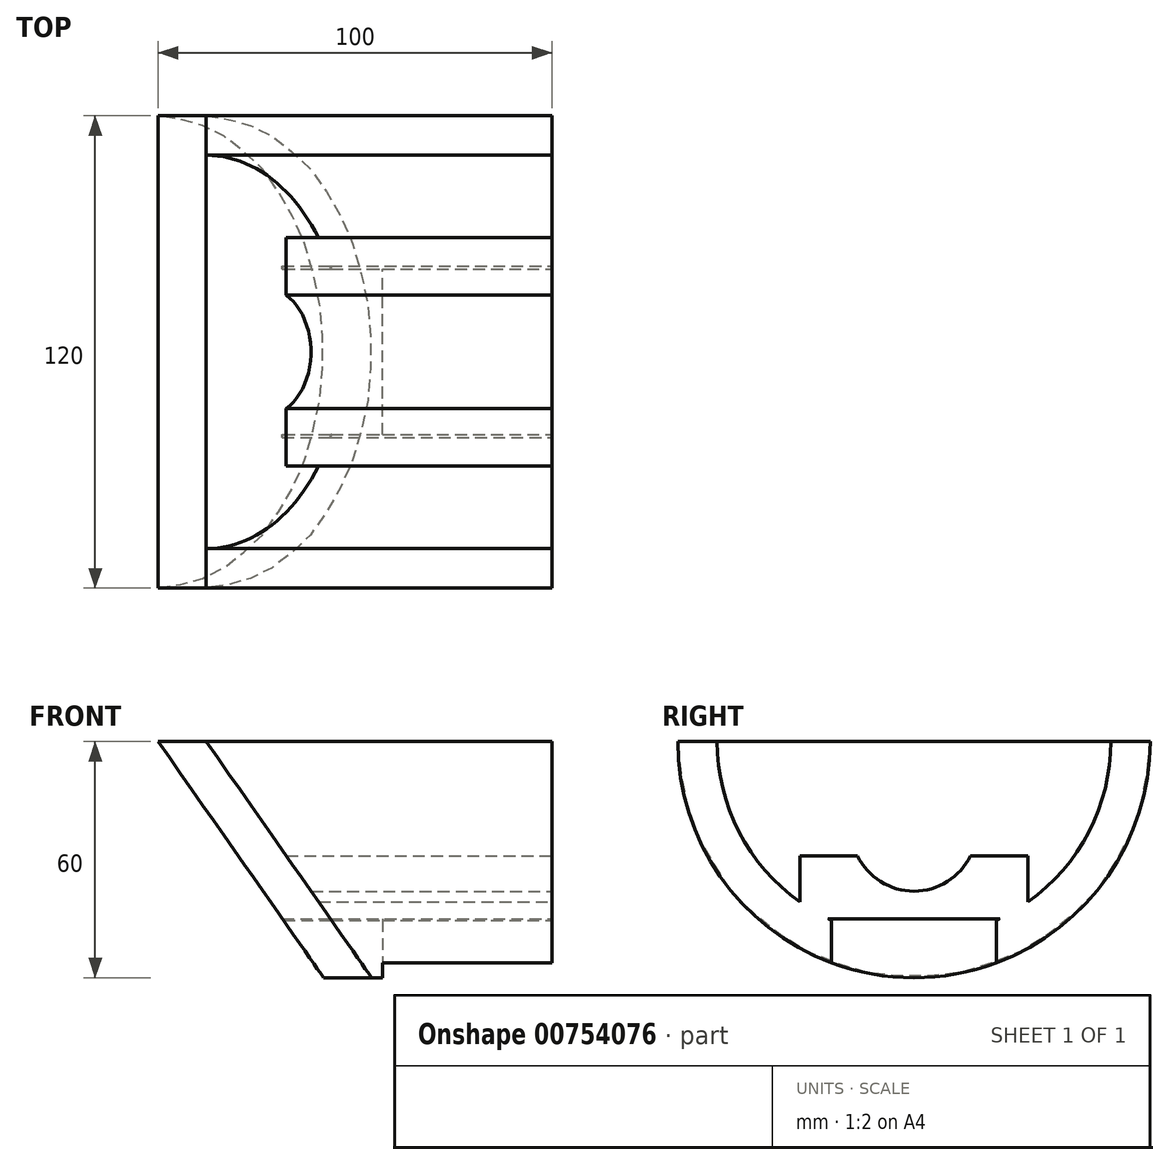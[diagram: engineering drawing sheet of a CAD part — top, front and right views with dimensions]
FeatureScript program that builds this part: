
annotation { "Feature Type Name" : "Feature", "Feature Type Description" : "" }
export const myFeature = defineFeature(function(context is Context, id is Id, definition is map)
    precondition{}
    {
        {
            var Q0;
            Q0=qCreatedBy(makeId("Right.planeOp"),FACE);
            var sketch = newSketch(context, id + "F0", { "sketchPlane" : qUnion([Q0])});
            skArc(sketch, "E0", {"start": v(-60, 0) * mm, "mid": v(0, -60) * mm, "end": v(60, 0) * mm});
            skArc(sketch, "E1", {"start": v(-50, 0) * mm, "mid": v(0, -50) * mm, "end": v(50, 0) * mm});
            skCircle(sketch, "E2", {"center": v(0, -22) * mm, "radius": 16 * mm});
            skLineSegment(sketch, "E3", {"start": v(-68.18, 0) * mm, "end": v(68.4, 0) * mm});
            skLineSegment(sketch, "E4", {"start": v(-38.6, -29) * mm, "end": v(41.93, -29) * mm});
            skLineSegment(sketch, "E5", {"start": v(-26.14, -45) * mm, "end": v(26.36, -45) * mm});
            skLineSegment(sketch, "E6", {"start": v(21, -45) * mm, "end": v(21, -63.96) * mm});
            skLineSegment(sketch, "E7", {"start": v(-21, -45) * mm, "end": v(-21, -64.85) * mm});
            skLineSegment(sketch, "E8", {"start": v(29, -29) * mm, "end": v(29, -49.1) * mm});
            skLineSegment(sketch, "E9", {"start": v(-29, -29) * mm, "end": v(-29, -49.67) * mm});
            skSolve(sketch);
        }
        {
            var Q0;
            {var subQ4=sQuery(id+"F0.wireOp",EDGE,"E0");var subQ7=sQuery(id+"F0.wireOp",EDGE,"E3");var subQ9=makeQuery(id+"F0.imprint","INTERSECT",VERTEX,{"disambiguationData":[OD(0.0)],"derivedFrom":[subQ4,subQ7]});Q0=makeQuery(id+"F0.imprint","IMPRINT",FACE,{"disambiguationData":[TD([[makeQuery(id+"F0.imprint","IMPRINT",EDGE,{"disambiguationData":[TD([[subQ9,-1.0]])],"derivedFrom":subQ4}),1.0]])]});}
            var Q1;
            {var subQ0=sQuery(id+"F0.wireOp",EDGE,"E9");var subQ7=sQuery(id+"F0.wireOp",EDGE,"E1");var subQ13=makeQuery(id+"F0.imprint","INTERSECT",VERTEX,{"derivedFrom":[subQ7,subQ0]});Q1=makeQuery(id+"F0.imprint","IMPRINT",FACE,{"disambiguationData":[TD([[makeQuery(id+"F0.imprint","IMPRINT",EDGE,{"disambiguationData":[TD([[subQ13,-1.0]])],"derivedFrom":subQ7}),1.0]])]});}
            var Q2;
            {var subQ6=sQuery(id+"F0.wireOp",EDGE,"E3");var subQ7=sQuery(id+"F0.wireOp",EDGE,"E0");var subQ8=makeQuery(id+"F0.imprint","INTERSECT",VERTEX,{"disambiguationData":[OD(1.0)],"derivedFrom":[subQ7,subQ6]});Q2=makeQuery(id+"F0.imprint","IMPRINT",FACE,{"disambiguationData":[TD([[makeQuery(id+"F0.imprint","IMPRINT",EDGE,{"disambiguationData":[TD([[subQ8,1.0]])],"derivedFrom":subQ7}),1.0]])]});}
            var Q3;
            {var subQ0=sQuery(id+"F0.wireOp",EDGE,"E5");var subQ1=sQuery(id+"F0.wireOp",EDGE,"E1");var subQ2=makeQuery(id+"F0.imprint","INTERSECT",VERTEX,{"disambiguationData":[OD(1.0)],"derivedFrom":[subQ1,subQ0]});Q3=makeQuery(id+"F0.imprint","IMPRINT",FACE,{"disambiguationData":[TD([[makeQuery(id+"F0.imprint","IMPRINT",EDGE,{"disambiguationData":[TD([[subQ2,1.0]])],"derivedFrom":subQ1}),1.0]])]});}
            var Q4;
            {var subQ0=sQuery(id+"F0.wireOp",EDGE,"E5");var subQ1=sQuery(id+"F0.wireOp",EDGE,"E1");var subQ2=makeQuery(id+"F0.imprint","INTERSECT",VERTEX,{"disambiguationData":[OD(0.0)],"derivedFrom":[subQ1,subQ0]});Q4=makeQuery(id+"F0.imprint","IMPRINT",FACE,{"disambiguationData":[TD([[makeQuery(id+"F0.imprint","IMPRINT",EDGE,{"disambiguationData":[TD([[subQ2,-1.0]])],"derivedFrom":subQ1}),1.0]])]});}
            var Q5;
            {var subQ0=sQuery(id+"F0.wireOp",EDGE,"E7");var subQ1=sQuery(id+"F0.wireOp",EDGE,"E1");var subQ2=makeQuery(id+"F0.imprint","INTERSECT",VERTEX,{"derivedFrom":[subQ1,subQ0]});Q5=makeQuery(id+"F0.imprint","IMPRINT",FACE,{"disambiguationData":[TD([[makeQuery(id+"F0.imprint","IMPRINT",EDGE,{"disambiguationData":[TD([[subQ2,-1.0]])],"derivedFrom":subQ1}),1.0]])]});}
            var Q6;
            {var subQ0=sQuery(id+"F0.wireOp",EDGE,"E7");var subQ1=sQuery(id+"F0.wireOp",EDGE,"E0");var subQ2=makeQuery(id+"F0.imprint","INTERSECT",VERTEX,{"derivedFrom":[subQ1,subQ0]});Q6=makeQuery(id+"F0.imprint","IMPRINT",FACE,{"disambiguationData":[TD([[makeQuery(id+"F0.imprint","IMPRINT",EDGE,{"disambiguationData":[TD([[subQ2,-1.0]])],"derivedFrom":subQ1}),1.0]])]});}
            extrude(context, id + "F1", {"entities" : qUnion([Q0, Q1, Q2, Q3, Q4, Q5, Q6]), "depth" : -100 * mm, "offsetDistance" : 25 * mm});
        }
        {
            var Q0;
            Q0=qCreatedBy(makeId("Front.planeOp"),FACE);
            var sketch = newSketch(context, id + "F2", { "sketchPlane" : qUnion([Q0])});
            skLineSegment(sketch, "E10.0", {"start": v(-100, 0) * mm, "end": v(0, 0) * mm});
            skLineSegment(sketch, "E11", {"start": v(-100, 0) * mm, "end": v(-56.9, -61.57) * mm});
            skLineSegment(sketch, "E12", {"start": v(0, -60) * mm, "end": v(-100, -60) * mm});
            skLineSegment(sketch, "E13.0", {"start": v(-91.8, 5.74) * mm, "end": v(-41.52, -66.08) * mm});
            skLineSegment(sketch, "E14", {"start": v(-41.52, -66.08) * mm, "end": v(-123.05, -66.08) * mm});
            skLineSegment(sketch, "E15", {"start": v(-123.05, -66.08) * mm, "end": v(-123.05, 5.74) * mm});
            skLineSegment(sketch, "E16", {"start": v(-123.05, 5.74) * mm, "end": v(-91.8, 5.74) * mm});
            skSolve(sketch);
        }
        {
            var Q0;
            {var subQ9=sQuery(id+"F2.wireOp",EDGE,"E14");Q0=makeQuery(id+"F2.imprint","IMPRINT",FACE,{"disambiguationData":[TD([[makeQuery(id+"F2.imprint","IMPRINT",EDGE,{"derivedFrom":subQ9}),-1.0]])]});}
            var Q1;
            {var subQ0=sQuery(id+"F2.wireOp",EDGE,"E11");var subQ1=sQuery(id+"F2.wireOp",EDGE,"E10.0");var subQ2=makeQuery(id+"F2.imprint","INTERSECT",VERTEX,{"derivedFrom":[subQ1,subQ0]});Q1=makeQuery(id+"F2.imprint","IMPRINT",FACE,{"disambiguationData":[TD([[makeQuery(id+"F2.imprint","IMPRINT",EDGE,{"disambiguationData":[TD([[subQ2,-1.0]])],"derivedFrom":subQ1}),-1.0]])]});}
            extrude(context, id + "F3", {"entities" : qUnion([Q0, Q1]), "operationType" : NewBodyOperationType.REMOVE, "oppositeDirection" : true, "depth" : 79.9 * mm, "offsetDistance" : 25 * mm, "hasSecondDirection" : true, "secondDirectionOppositeDirection" : false, "secondDirectionDepth" : 98 * mm});
        }
        {
            var Q0;
            {var subQ0=sQuery(id+"F0.wireOp",EDGE,"E3");Q0=makeQuery(id+"F3.boolean.opBoolean","INTERSECT",EDGE,{"derivedFrom":[makeQuery(id+"F1.opExtrude","SWEPT_FACE",FACE,{"disambiguationData":[OSD([subQ0]),TDD([makeQuery(id+"F0.imprint","IMPRINT",EDGE,{"disambiguationData":[TD([[makeQuery(id+"F0.imprint","INTERSECT",VERTEX,{"disambiguationData":[OD(1.0)],"derivedFrom":[sQuery(id+"F0.wireOp",EDGE,"E0"),subQ0]}),1.0]])],"derivedFrom":subQ0})])]}),makeQuery(id+"F3.opExtrude","SWEPT_FACE",FACE,{"disambiguationData":[OSD([sQuery(id+"F2.wireOp",EDGE,"E13.0")])]})]});}
            cPlane(context, id + "F4", {"entities" : qUnion([Q0]), "cplaneType" : CPlaneType.LINE_ANGLE, "offset" : 25 * mm, "angle" : 125 * degree, "oppositeDirection" : true, "width" : 150 * mm, "height" : 150 * mm});
        }
        {
            var Q0;
            Q0=qCreatedBy(makeId("Front.planeOp"),FACE);
            var sketch = newSketch(context, id + "F5", { "sketchPlane" : qUnion([Q0])});
            skLineSegment(sketch, "E17.0", {"start": v(-91.8, 5.74) * mm, "end": v(-41.52, -66.08) * mm});
            skLineSegment(sketch, "E18.0", {"start": v(-100, 0) * mm, "end": v(-56.9, -61.57) * mm});
            skLineSegment(sketch, "E19", {"start": v(-56.9, -61.57) * mm, "end": v(-53.73, -66.08) * mm});
            skLineSegment(sketch, "E20", {"start": v(-53.73, -66.08) * mm, "end": v(-41.52, -66.08) * mm});
            skLineSegment(sketch, "E21", {"start": v(-100, 0) * mm, "end": v(-104.02, 5.74) * mm});
            skLineSegment(sketch, "E22", {"start": v(-104.02, 5.74) * mm, "end": v(-91.8, 5.74) * mm});
            skSolve(sketch);
        }
        {
            var Q0;
            Q0=makeQuery(id+"F5.imprint","IMPRINT",FACE,{"disambiguationData":[TD([[makeQuery(id+"F5.imprint","IMPRINT",EDGE,{"derivedFrom":sQuery(id+"F5.wireOp",EDGE,"E17.0")}),-1.0]])]});
            extrude(context, id + "F6", {"entities" : qUnion([Q0]), "depth" : 74.8 * mm, "offsetDistance" : 25 * mm, "hasSecondDirection" : true, "secondDirectionOppositeDirection" : true, "secondDirectionDepth" : 93.6 * mm});
        }
        {
            var Q0;
            {var subQ4=sQuery(id+"F0.wireOp",EDGE,"E0");var subQ7=sQuery(id+"F0.wireOp",EDGE,"E3");var subQ9=makeQuery(id+"F0.imprint","INTERSECT",VERTEX,{"disambiguationData":[OD(0.0)],"derivedFrom":[subQ4,subQ7]});Q0=makeQuery(id+"F0.imprint","IMPRINT",FACE,{"disambiguationData":[TD([[makeQuery(id+"F0.imprint","IMPRINT",EDGE,{"disambiguationData":[TD([[subQ9,-1.0]])],"derivedFrom":subQ4}),1.0]])]});}
            var Q1;
            {var subQ0=sQuery(id+"F0.wireOp",EDGE,"E3");var subQ1=sQuery(id+"F0.wireOp",EDGE,"E1");var subQ2=makeQuery(id+"F0.imprint","INTERSECT",VERTEX,{"disambiguationData":[OD(0.0)],"derivedFrom":[subQ1,subQ0]});Q1=makeQuery(id+"F0.imprint","IMPRINT",FACE,{"disambiguationData":[TD([[makeQuery(id+"F0.imprint","IMPRINT",EDGE,{"disambiguationData":[TD([[subQ2,-1.0]])],"derivedFrom":subQ1}),1.0]])]});}
            var Q2;
            {var subQ0=sQuery(id+"F0.wireOp",EDGE,"E4");var subQ1=sQuery(id+"F0.wireOp",EDGE,"E2");var subQ2=makeQuery(id+"F0.imprint","INTERSECT",VERTEX,{"disambiguationData":[OD(0.0)],"derivedFrom":[subQ1,subQ0]});Q2=makeQuery(id+"F0.imprint","IMPRINT",FACE,{"disambiguationData":[TD([[makeQuery(id+"F0.imprint","IMPRINT",EDGE,{"disambiguationData":[TD([[subQ2,1.0]])],"derivedFrom":subQ1}),1.0]])]});}
            var Q3;
            {var subQ6=sQuery(id+"F0.wireOp",EDGE,"E3");var subQ7=sQuery(id+"F0.wireOp",EDGE,"E0");var subQ8=makeQuery(id+"F0.imprint","INTERSECT",VERTEX,{"disambiguationData":[OD(1.0)],"derivedFrom":[subQ7,subQ6]});Q3=makeQuery(id+"F0.imprint","IMPRINT",FACE,{"disambiguationData":[TD([[makeQuery(id+"F0.imprint","IMPRINT",EDGE,{"disambiguationData":[TD([[subQ8,1.0]])],"derivedFrom":subQ7}),1.0]])]});}
            var Q4;
            {var subQ0=sQuery(id+"F0.wireOp",EDGE,"E4");var subQ1=sQuery(id+"F0.wireOp",EDGE,"E2");var subQ2=makeQuery(id+"F0.imprint","INTERSECT",VERTEX,{"disambiguationData":[OD(0.0)],"derivedFrom":[subQ1,subQ0]});Q4=makeQuery(id+"F0.imprint","IMPRINT",FACE,{"disambiguationData":[TD([[makeQuery(id+"F0.imprint","IMPRINT",EDGE,{"disambiguationData":[TD([[subQ2,-1.0]])],"derivedFrom":subQ1}),1.0]])]});}
            var Q5;
            {var subQ0=sQuery(id+"F0.wireOp",EDGE,"E9");var subQ7=sQuery(id+"F0.wireOp",EDGE,"E1");var subQ13=makeQuery(id+"F0.imprint","INTERSECT",VERTEX,{"derivedFrom":[subQ7,subQ0]});Q5=makeQuery(id+"F0.imprint","IMPRINT",FACE,{"disambiguationData":[TD([[makeQuery(id+"F0.imprint","IMPRINT",EDGE,{"disambiguationData":[TD([[subQ13,-1.0]])],"derivedFrom":subQ7}),1.0]])]});}
            var Q6;
            {var subQ0=sQuery(id+"F0.wireOp",EDGE,"E8");var subQ1=sQuery(id+"F0.wireOp",EDGE,"E1");var subQ2=makeQuery(id+"F0.imprint","INTERSECT",VERTEX,{"derivedFrom":[subQ1,subQ0]});Q6=makeQuery(id+"F0.imprint","IMPRINT",FACE,{"disambiguationData":[TD([[makeQuery(id+"F0.imprint","IMPRINT",EDGE,{"disambiguationData":[TD([[subQ2,-1.0]])],"derivedFrom":subQ1}),1.0]])]});}
            var Q7;
            {var subQ0=sQuery(id+"F0.wireOp",EDGE,"E7");var subQ1=sQuery(id+"F0.wireOp",EDGE,"E1");var subQ2=makeQuery(id+"F0.imprint","INTERSECT",VERTEX,{"derivedFrom":[subQ1,subQ0]});Q7=makeQuery(id+"F0.imprint","IMPRINT",FACE,{"disambiguationData":[TD([[makeQuery(id+"F0.imprint","IMPRINT",EDGE,{"disambiguationData":[TD([[subQ2,-1.0]])],"derivedFrom":subQ1}),1.0]])]});}
            var Q8;
            {var subQ0=sQuery(id+"F0.wireOp",EDGE,"E7");var subQ1=sQuery(id+"F0.wireOp",EDGE,"E0");var subQ2=makeQuery(id+"F0.imprint","INTERSECT",VERTEX,{"derivedFrom":[subQ1,subQ0]});Q8=makeQuery(id+"F0.imprint","IMPRINT",FACE,{"disambiguationData":[TD([[makeQuery(id+"F0.imprint","IMPRINT",EDGE,{"disambiguationData":[TD([[subQ2,-1.0]])],"derivedFrom":subQ1}),1.0]])]});}
            var Q9;
            {var subQ0=sQuery(id+"F0.wireOp",EDGE,"E5");var subQ1=sQuery(id+"F0.wireOp",EDGE,"E1");var subQ2=makeQuery(id+"F0.imprint","INTERSECT",VERTEX,{"disambiguationData":[OD(1.0)],"derivedFrom":[subQ1,subQ0]});Q9=makeQuery(id+"F0.imprint","IMPRINT",FACE,{"disambiguationData":[TD([[makeQuery(id+"F0.imprint","IMPRINT",EDGE,{"disambiguationData":[TD([[subQ2,1.0]])],"derivedFrom":subQ1}),1.0]])]});}
            var Q10;
            {var subQ0=sQuery(id+"F0.wireOp",EDGE,"E5");var subQ1=sQuery(id+"F0.wireOp",EDGE,"E1");var subQ2=makeQuery(id+"F0.imprint","INTERSECT",VERTEX,{"disambiguationData":[OD(0.0)],"derivedFrom":[subQ1,subQ0]});Q10=makeQuery(id+"F0.imprint","IMPRINT",FACE,{"disambiguationData":[TD([[makeQuery(id+"F0.imprint","IMPRINT",EDGE,{"disambiguationData":[TD([[subQ2,-1.0]])],"derivedFrom":subQ1}),1.0]])]});}
            extrude(context, id + "F7", {"entities" : qUnion([Q0, Q1, Q2, Q3, Q4, Q5, Q6, Q7, Q8, Q9, Q10]), "operationType" : NewBodyOperationType.INTERSECT, "oppositeDirection" : true, "depth" : 115.8 * mm, "offsetDistance" : 25 * mm});
        }
        {
            var Q0;
            {var subQ0=sQuery(id+"F0.wireOp",EDGE,"E7");var subQ1=sQuery(id+"F0.wireOp",EDGE,"E1");var subQ2=makeQuery(id+"F0.imprint","INTERSECT",VERTEX,{"derivedFrom":[subQ1,subQ0]});Q0=makeQuery(id+"F0.imprint","IMPRINT",FACE,{"disambiguationData":[TD([[makeQuery(id+"F0.imprint","IMPRINT",EDGE,{"disambiguationData":[TD([[subQ2,-1.0]])],"derivedFrom":subQ1}),1.0]])]});}
            var Q1;
            {var subQ0=sQuery(id+"F0.wireOp",EDGE,"E7");var subQ1=sQuery(id+"F0.wireOp",EDGE,"E0");var subQ2=makeQuery(id+"F0.imprint","INTERSECT",VERTEX,{"derivedFrom":[subQ1,subQ0]});Q1=makeQuery(id+"F0.imprint","IMPRINT",FACE,{"disambiguationData":[TD([[makeQuery(id+"F0.imprint","IMPRINT",EDGE,{"disambiguationData":[TD([[subQ2,-1.0]])],"derivedFrom":subQ1}),1.0]])]});}
            extrude(context, id + "F8", {"entities" : qUnion([Q0, Q1]), "operationType" : NewBodyOperationType.REMOVE, "oppositeDirection" : true, "depth" : 43 * mm, "offsetDistance" : 25 * mm});
        }
    });
